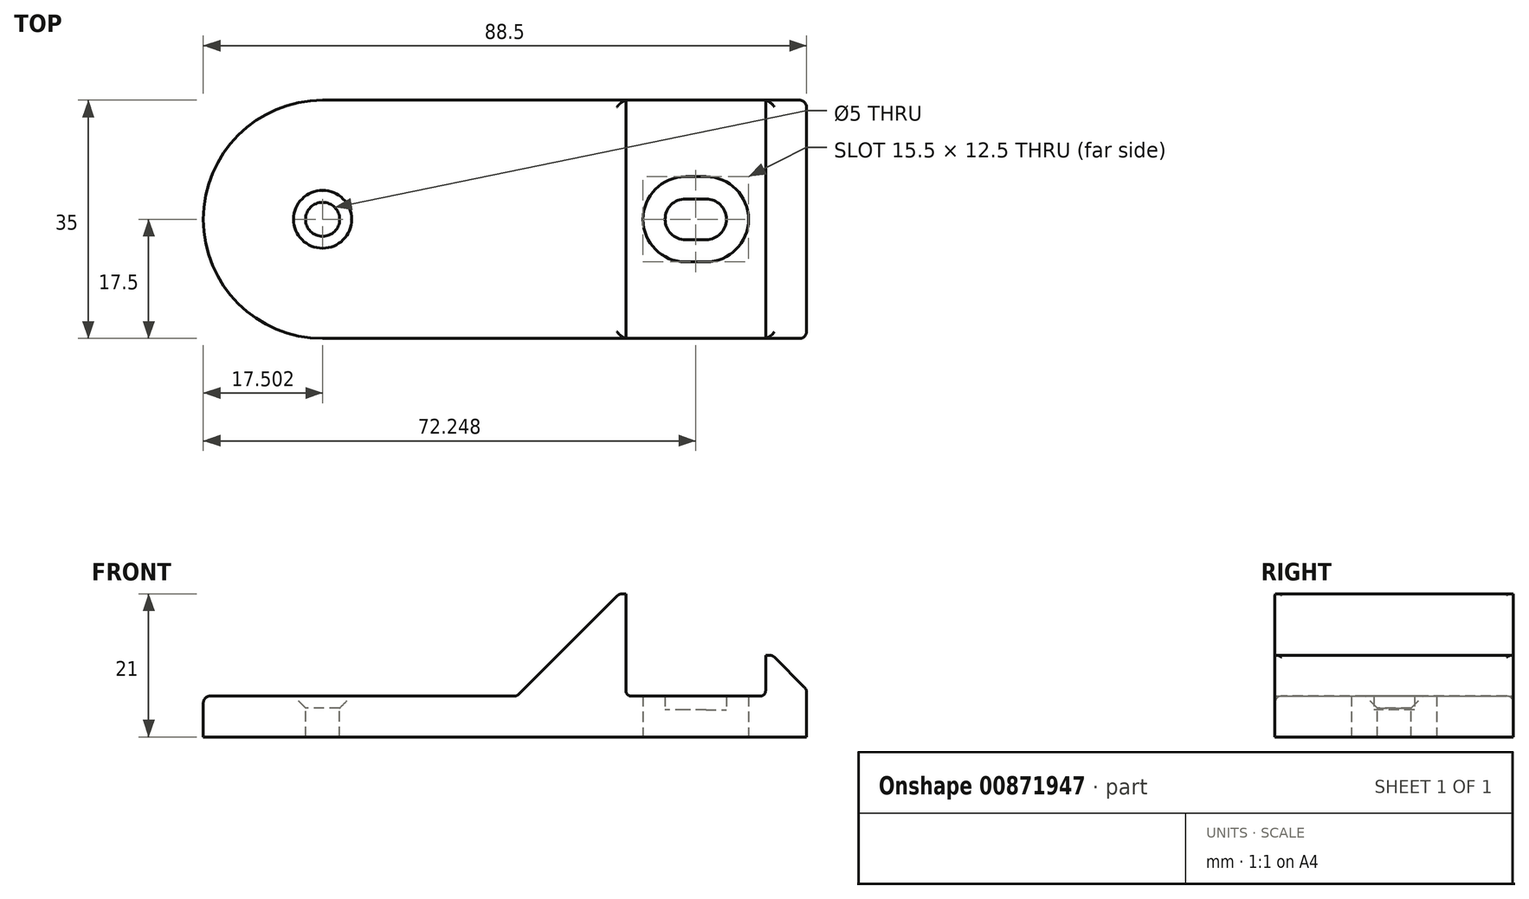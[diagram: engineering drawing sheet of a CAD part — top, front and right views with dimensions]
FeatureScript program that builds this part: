
annotation { "Feature Type Name" : "Feature", "Feature Type Description" : "" }
export const myFeature = defineFeature(function(context is Context, id is Id, definition is map)
    precondition{}
    {
        {
            var Q0;
            Q0=qCreatedBy(makeId("Top.planeOp"),FACE);
            var sketch = newSketch(context, id + "F0", { "sketchPlane" : qUnion([Q0])});
            skLineSegment(sketch, "E0", {"start": v(-55.44, 0) * mm, "end": v(55.68, 0) * mm, "construction": true});
            skLineSegment(sketch, "E1", {"start": v(0, 54) * mm, "end": v(0, -52.34) * mm, "construction": true});
            skLineSegment(sketch, "E2.bottom", {"start": v(-35.65, 17.5) * mm, "end": v(29.35, 17.5) * mm});
            skLineSegment(sketch, "E2.top", {"start": v(-35.65, -17.5) * mm, "end": v(29.35, -17.5) * mm});
            skLineSegment(sketch, "E2.left", {"start": v(-35.65, 17.5) * mm, "end": v(-35.65, -17.5) * mm});
            skLineSegment(sketch, "E2.right", {"start": v(29.35, 17.5) * mm, "end": v(29.35, -17.5) * mm});
            skPoint(sketch, "E3", {"position": v(-35.65, 0) * mm});
            skArc(sketch, "E4", {"start": v(-35.65, -17.5) * mm, "mid": v(-53.15, 0) * mm, "end": v(-35.65, 17.5) * mm});
            skLineSegment(sketch, "E5.bottom", {"start": v(29.35, 17.5) * mm, "end": v(35.35, 17.5) * mm});
            skLineSegment(sketch, "E5.top", {"start": v(29.35, -17.5) * mm, "end": v(35.35, -17.5) * mm});
            skLineSegment(sketch, "E5.right", {"start": v(35.35, 17.5) * mm, "end": v(35.35, -17.5) * mm});
            skLineSegment(sketch, "E6.bottom", {"start": v(8.85, 17.5) * mm, "end": v(2.85, 17.5) * mm});
            skLineSegment(sketch, "E6.top", {"start": v(8.85, -17.5) * mm, "end": v(2.85, -17.5) * mm});
            skLineSegment(sketch, "E6.left", {"start": v(8.85, 17.5) * mm, "end": v(8.85, -17.5) * mm});
            skLineSegment(sketch, "E6.right", {"start": v(2.85, 17.5) * mm, "end": v(2.85, -17.5) * mm});
            skSolve(sketch);
        }
        {
            var Q0;
            {var subQ0=sQuery(id+"F0.wireOp",EDGE,"E6.left");var subQ5=makeQuery(id+"F0.imprint","IMPRINT",EDGE,{"derivedFrom":subQ0});var subQ11=sQuery(id+"F0.wireOp",EDGE,"E2.right");var subQ13=makeQuery(id+"F0.imprint","IMPRINT",EDGE,{"derivedFrom":subQ11});var subQ15=sQuery(id+"F0.wireOp",EDGE,"E2.left");var subQ16=makeQuery(id+"F0.imprint","IMPRINT",EDGE,{"derivedFrom":subQ15});Q0=qUnion([makeQuery(id+"F0.imprint","IMPRINT",FACE,{"disambiguationData":[TD([[subQ16,-1.0]])]}),makeQuery(id+"F0.imprint","IMPRINT",FACE,{"disambiguationData":[TD([[subQ13,1.0]])]}),makeQuery(id+"F0.imprint","IMPRINT",FACE,{"disambiguationData":[TD([[subQ16,1.0]])]}),makeQuery(id+"F0.imprint","IMPRINT",FACE,{"disambiguationData":[TD([[subQ13,-1.0]])]}),makeQuery(id+"F0.imprint","IMPRINT",FACE,{"disambiguationData":[TD([[subQ5,-1.0]])]})]);}
            extrude(context, id + "F1", {"entities" : qUnion([Q0]), "depth" : 6 * mm, "offsetDistance" : 25 * mm});
        }
        {
            var Q0;
            Q0=makeQuery(id+"F0.imprint","IMPRINT",FACE,{"disambiguationData":[TD([[makeQuery(id+"F0.imprint","IMPRINT",EDGE,{"derivedFrom":sQuery(id+"F0.wireOp",EDGE,"E2.right")}),1.0]])]});
            extrude(context, id + "F2", {"entities" : qUnion([Q0]), "operationType" : NewBodyOperationType.ADD, "depth" : 12 * mm, "offsetDistance" : 25 * mm});
        }
        {
            var Q0;
            Q0=makeQuery(id+"F2.opExtrude","CAP_EDGE",EDGE,{"disambiguationData":[OSD([sQuery(id+"F0.wireOp",EDGE,"E5.right")])],"isStart":false});
            chamfer(context, id + "F3", {"entities" : qUnion([Q0]), "width" : 5 * mm, "tangentPropagation" : true});
        }
        {
            var Q0;
            {var subQ0=sQuery(id+"F0.wireOp",EDGE,"E6.left");Q0=makeQuery(id+"F0.imprint","IMPRINT",FACE,{"disambiguationData":[TD([[makeQuery(id+"F0.imprint","IMPRINT",EDGE,{"derivedFrom":subQ0}),-1.0]])]});}
            extrude(context, id + "F4", {"entities" : qUnion([Q0]), "operationType" : NewBodyOperationType.ADD, "depth" : 21 * mm, "offsetDistance" : 25 * mm});
        }
        {
            var Q0;
            Q0=makeQuery(id+"F4.opExtrude","CAP_EDGE",EDGE,{"disambiguationData":[OSD([sQuery(id+"F0.wireOp",EDGE,"E6.right")])],"isStart":false});
            chamfer(context, id + "F5", {"entities" : qUnion([Q0]), "width" : 5 * mm, "tangentPropagation" : true});
        }
        {
            var Q0;
            Q0=makeQuery(id+"F4.opExtrude","SWEPT_FACE",FACE,{"disambiguationData":[OSD([sQuery(id+"F0.wireOp",EDGE,"E6.right")])]});
            extrude(context, id + "F6", {"entities" : qUnion([Q0]), "operationType" : NewBodyOperationType.ADD, "depth" : 12 * mm, "offsetDistance" : 25 * mm});
        }
        {
            var Q0;
            Q0=makeQuery(id+"F6.opExtrude","CAP_EDGE",EDGE,{"disambiguationData":[OSD([sQuery(id+"F0.wireOp",EDGE,"E6.right")])],"isStart":false});
            chamfer(context, id + "F7", {"entities" : qUnion([Q0]), "width" : 12 * mm, "tangentPropagation" : true});
        }
        {
            var Q0;
            {var subQ0=sQuery(id+"F0.wireOp",EDGE,"E5.top");var subQ1=sQuery(id+"F0.wireOp",EDGE,"E2.top");var subQ2=sQuery(id+"F0.wireOp",EDGE,"E4");Q0=makeQuery(id+"F4.boolean.opBoolean","SPLIT",EDGE,{"disambiguationData":[TD([makeQuery(id+"F1.opExtrude","SWEPT_FACE",FACE,{"disambiguationData":[OSD([subQ2])]})])],"derivedFrom":makeQuery(id+"F1.opExtrude","CAP_EDGE",EDGE,{"disambiguationData":[OSD([subQ1,subQ0])],"isStart":false})});}
            var Q1;
            {var subQ0=sQuery(id+"F0.wireOp",EDGE,"E5.right");var subQ1=sQuery(id+"F0.wireOp",EDGE,"E5.top");Q1=makeQuery(id+"F2.boolean.opBoolean","MERGE",EDGE,{"derivedFrom":[makeQuery(id+"F1.opExtrude","SWEPT_EDGE",EDGE,{"disambiguationData":[OSD([subQ1,subQ0])]}),makeQuery(id+"F2.opExtrude","SWEPT_EDGE",EDGE,{"disambiguationData":[OSD([subQ1,subQ0])]})]});}
            var Q2;
            {var subQ0=sQuery(id+"F0.wireOp",EDGE,"E5.top");Q2=makeQuery(id+"F3.opChamfer","BLEND_EDGE",EDGE,{"blendedFrom":[makeQuery(id+"F2.opExtrude","CAP_EDGE",EDGE,{"disambiguationData":[OSD([sQuery(id+"F0.wireOp",EDGE,"E5.right")])],"isStart":false}),makeQuery(id+"F2.boolean.opBoolean","MERGE",FACE,{"derivedFrom":[makeQuery(id+"F1.opExtrude","SWEPT_FACE",FACE,{"disambiguationData":[OSD([sQuery(id+"F0.wireOp",EDGE,"E2.top"),subQ0])]}),makeQuery(id+"F2.opExtrude","SWEPT_FACE",FACE,{"disambiguationData":[OSD([subQ0])]})]})],"blendedInto":[makeQuery(id+"F2.boolean.opBoolean","MERGE",FACE,{"derivedFrom":[makeQuery(id+"F1.opExtrude","SWEPT_FACE",FACE,{"disambiguationData":[OSD([sQuery(id+"F0.wireOp",EDGE,"E2.top"),subQ0])]}),makeQuery(id+"F2.opExtrude","SWEPT_FACE",FACE,{"disambiguationData":[OSD([subQ0])]})]})]});}
            var Q3;
            {var subQ0=sQuery(id+"F0.wireOp",EDGE,"E5.right");Q3=makeQuery(id+"F3.opChamfer","BLEND_EDGE",EDGE,{"blendedFrom":[makeQuery(id+"F2.opExtrude","CAP_EDGE",EDGE,{"disambiguationData":[OSD([subQ0])],"isStart":false}),makeQuery(id+"F2.boolean.opBoolean","MERGE",FACE,{"derivedFrom":[makeQuery(id+"F1.opExtrude","SWEPT_FACE",FACE,{"disambiguationData":[OSD([subQ0])]}),makeQuery(id+"F2.opExtrude","SWEPT_FACE",FACE,{"disambiguationData":[OSD([subQ0])]})]})],"blendedInto":[makeQuery(id+"F2.boolean.opBoolean","MERGE",FACE,{"derivedFrom":[makeQuery(id+"F1.opExtrude","SWEPT_FACE",FACE,{"disambiguationData":[OSD([subQ0])]}),makeQuery(id+"F2.opExtrude","SWEPT_FACE",FACE,{"disambiguationData":[OSD([subQ0])]})]})]});}
            var Q4;
            {var subQ0=sQuery(id+"F0.wireOp",EDGE,"E5.bottom");Q4=makeQuery(id+"F3.opChamfer","BLEND_EDGE",EDGE,{"blendedFrom":[makeQuery(id+"F2.opExtrude","CAP_EDGE",EDGE,{"disambiguationData":[OSD([sQuery(id+"F0.wireOp",EDGE,"E5.right")])],"isStart":false}),makeQuery(id+"F2.boolean.opBoolean","MERGE",FACE,{"derivedFrom":[makeQuery(id+"F1.opExtrude","SWEPT_FACE",FACE,{"disambiguationData":[OSD([sQuery(id+"F0.wireOp",EDGE,"E2.bottom"),subQ0])]}),makeQuery(id+"F2.opExtrude","SWEPT_FACE",FACE,{"disambiguationData":[OSD([subQ0])]})]})],"blendedInto":[makeQuery(id+"F2.boolean.opBoolean","MERGE",FACE,{"derivedFrom":[makeQuery(id+"F1.opExtrude","SWEPT_FACE",FACE,{"disambiguationData":[OSD([sQuery(id+"F0.wireOp",EDGE,"E2.bottom"),subQ0])]}),makeQuery(id+"F2.opExtrude","SWEPT_FACE",FACE,{"disambiguationData":[OSD([subQ0])]})]})]});}
            var Q5;
            {var subQ0=sQuery(id+"F0.wireOp",EDGE,"E5.right");var subQ1=sQuery(id+"F0.wireOp",EDGE,"E5.bottom");Q5=makeQuery(id+"F2.boolean.opBoolean","MERGE",EDGE,{"derivedFrom":[makeQuery(id+"F1.opExtrude","SWEPT_EDGE",EDGE,{"disambiguationData":[OSD([subQ1,subQ0])]}),makeQuery(id+"F2.opExtrude","SWEPT_EDGE",EDGE,{"disambiguationData":[OSD([subQ1,subQ0])]})]});}
            var Q6;
            {var subQ0=sQuery(id+"F0.wireOp",EDGE,"E6.right");var subQ1=sQuery(id+"F0.wireOp",EDGE,"E2.top");var subQ2=sQuery(id+"F0.wireOp",EDGE,"E5.top");Q6=makeQuery(id+"F7.opChamfer","BLEND_EDGE",EDGE,{"blendedFrom":[makeQuery(id+"F6.opExtrude","CAP_EDGE",EDGE,{"disambiguationData":[OSD([subQ0])],"isStart":false}),makeQuery(id+"F6.boolean.opBoolean","MERGE",FACE,{"derivedFrom":[makeQuery(id+"F4.boolean.opBoolean","MERGE",FACE,{"derivedFrom":[makeQuery(id+"F2.boolean.opBoolean","MERGE",FACE,{"derivedFrom":[makeQuery(id+"F1.opExtrude","SWEPT_FACE",FACE,{"disambiguationData":[OSD([subQ1,subQ2])]}),makeQuery(id+"F2.opExtrude","SWEPT_FACE",FACE,{"disambiguationData":[OSD([subQ2])]})]}),makeQuery(id+"F4.opExtrude","SWEPT_FACE",FACE,{"disambiguationData":[OSD([subQ1])]})]}),makeQuery(id+"F6.opExtrude","SWEPT_FACE",FACE,{"disambiguationData":[OSD([subQ1,subQ0])]})]})],"blendedInto":[makeQuery(id+"F6.boolean.opBoolean","MERGE",FACE,{"derivedFrom":[makeQuery(id+"F4.boolean.opBoolean","MERGE",FACE,{"derivedFrom":[makeQuery(id+"F2.boolean.opBoolean","MERGE",FACE,{"derivedFrom":[makeQuery(id+"F1.opExtrude","SWEPT_FACE",FACE,{"disambiguationData":[OSD([subQ1,subQ2])]}),makeQuery(id+"F2.opExtrude","SWEPT_FACE",FACE,{"disambiguationData":[OSD([subQ2])]})]}),makeQuery(id+"F4.opExtrude","SWEPT_FACE",FACE,{"disambiguationData":[OSD([subQ1])]})]}),makeQuery(id+"F6.opExtrude","SWEPT_FACE",FACE,{"disambiguationData":[OSD([subQ1,subQ0])]})]})]});}
            var Q7;
            {var subQ0=sQuery(id+"F0.wireOp",EDGE,"E6.right");var subQ1=sQuery(id+"F0.wireOp",EDGE,"E2.bottom");var subQ2=sQuery(id+"F0.wireOp",EDGE,"E5.bottom");Q7=makeQuery(id+"F7.opChamfer","BLEND_EDGE",EDGE,{"blendedFrom":[makeQuery(id+"F6.opExtrude","CAP_EDGE",EDGE,{"disambiguationData":[OSD([subQ0])],"isStart":false}),makeQuery(id+"F6.boolean.opBoolean","MERGE",FACE,{"derivedFrom":[makeQuery(id+"F4.boolean.opBoolean","MERGE",FACE,{"derivedFrom":[makeQuery(id+"F2.boolean.opBoolean","MERGE",FACE,{"derivedFrom":[makeQuery(id+"F1.opExtrude","SWEPT_FACE",FACE,{"disambiguationData":[OSD([subQ1,subQ2])]}),makeQuery(id+"F2.opExtrude","SWEPT_FACE",FACE,{"disambiguationData":[OSD([subQ2])]})]}),makeQuery(id+"F4.opExtrude","SWEPT_FACE",FACE,{"disambiguationData":[OSD([subQ1])]})]}),makeQuery(id+"F6.opExtrude","SWEPT_FACE",FACE,{"disambiguationData":[OSD([subQ1,subQ0])]})]})],"blendedInto":[makeQuery(id+"F6.boolean.opBoolean","MERGE",FACE,{"derivedFrom":[makeQuery(id+"F4.boolean.opBoolean","MERGE",FACE,{"derivedFrom":[makeQuery(id+"F2.boolean.opBoolean","MERGE",FACE,{"derivedFrom":[makeQuery(id+"F1.opExtrude","SWEPT_FACE",FACE,{"disambiguationData":[OSD([subQ1,subQ2])]}),makeQuery(id+"F2.opExtrude","SWEPT_FACE",FACE,{"disambiguationData":[OSD([subQ2])]})]}),makeQuery(id+"F4.opExtrude","SWEPT_FACE",FACE,{"disambiguationData":[OSD([subQ1])]})]}),makeQuery(id+"F6.opExtrude","SWEPT_FACE",FACE,{"disambiguationData":[OSD([subQ1,subQ0])]})]})]});}
            var Q8;
            {var subQ0=sQuery(id+"F0.wireOp",EDGE,"E2.bottom");var subQ1=sQuery(id+"F0.wireOp",EDGE,"E5.bottom");Q8=makeQuery(id+"F5.opChamfer","BLEND_EDGE",EDGE,{"blendedFrom":[makeQuery(id+"F4.opExtrude","CAP_EDGE",EDGE,{"disambiguationData":[OSD([sQuery(id+"F0.wireOp",EDGE,"E6.right")])],"isStart":false}),makeQuery(id+"F4.boolean.opBoolean","MERGE",FACE,{"derivedFrom":[makeQuery(id+"F2.boolean.opBoolean","MERGE",FACE,{"derivedFrom":[makeQuery(id+"F1.opExtrude","SWEPT_FACE",FACE,{"disambiguationData":[OSD([subQ0,subQ1])]}),makeQuery(id+"F2.opExtrude","SWEPT_FACE",FACE,{"disambiguationData":[OSD([subQ1])]})]}),makeQuery(id+"F4.opExtrude","SWEPT_FACE",FACE,{"disambiguationData":[OSD([subQ0])]})]})],"blendedInto":[makeQuery(id+"F4.boolean.opBoolean","MERGE",FACE,{"derivedFrom":[makeQuery(id+"F2.boolean.opBoolean","MERGE",FACE,{"derivedFrom":[makeQuery(id+"F1.opExtrude","SWEPT_FACE",FACE,{"disambiguationData":[OSD([subQ0,subQ1])]}),makeQuery(id+"F2.opExtrude","SWEPT_FACE",FACE,{"disambiguationData":[OSD([subQ1])]})]}),makeQuery(id+"F4.opExtrude","SWEPT_FACE",FACE,{"disambiguationData":[OSD([subQ0])]})]})]});}
            var Q9;
            {var subQ0=sQuery(id+"F0.wireOp",EDGE,"E5.right");Q9=makeQuery(id+"F3.opChamfer","BLEND_EDGE",EDGE,{"blendedFrom":[makeQuery(id+"F2.opExtrude","CAP_EDGE",EDGE,{"disambiguationData":[OSD([subQ0])],"isStart":false}),makeQuery(id+"F2.opExtrude","CAP_FACE",FACE,{"disambiguationData":[OSD([sQuery(id+"F0.wireOp",EDGE,"E2.right"),sQuery(id+"F0.wireOp",EDGE,"E5.bottom"),sQuery(id+"F0.wireOp",EDGE,"E5.top"),subQ0])],"isStart":false})],"blendedInto":[makeQuery(id+"F2.opExtrude","CAP_FACE",FACE,{"disambiguationData":[OSD([sQuery(id+"F0.wireOp",EDGE,"E2.right"),sQuery(id+"F0.wireOp",EDGE,"E5.bottom"),sQuery(id+"F0.wireOp",EDGE,"E5.top"),subQ0])],"isStart":false})]});}
            var Q10;
            {var subQ0=sQuery(id+"F0.wireOp",EDGE,"E6.right");Q10=makeQuery(id+"F5.opChamfer","BLEND_EDGE",EDGE,{"blendedFrom":[makeQuery(id+"F4.opExtrude","CAP_EDGE",EDGE,{"disambiguationData":[OSD([subQ0])],"isStart":false}),makeQuery(id+"F4.opExtrude","CAP_FACE",FACE,{"disambiguationData":[OSD([sQuery(id+"F0.wireOp",EDGE,"E2.bottom"),sQuery(id+"F0.wireOp",EDGE,"E2.top"),sQuery(id+"F0.wireOp",EDGE,"E6.left"),subQ0])],"isStart":false})],"blendedInto":[makeQuery(id+"F4.opExtrude","CAP_FACE",FACE,{"disambiguationData":[OSD([sQuery(id+"F0.wireOp",EDGE,"E2.bottom"),sQuery(id+"F0.wireOp",EDGE,"E2.top"),sQuery(id+"F0.wireOp",EDGE,"E6.left"),subQ0])],"isStart":false})]});}
            var Q11;
            {var subQ0=sQuery(id+"F0.wireOp",EDGE,"E5.bottom");var subQ1=sQuery(id+"F0.wireOp",EDGE,"E4");var subQ2=sQuery(id+"F0.wireOp",EDGE,"E5.top");var subQ3=sQuery(id+"F0.wireOp",EDGE,"E2.top");var subQ4=sQuery(id+"F0.wireOp",EDGE,"E2.bottom");var subQ5=sQuery(id+"F0.wireOp",EDGE,"E6.right");Q11=makeQuery(id+"F7.opChamfer","BLEND_EDGE",EDGE,{"blendedFrom":[makeQuery(id+"F6.opExtrude","CAP_EDGE",EDGE,{"disambiguationData":[OSD([subQ5])],"isStart":false}),makeQuery(id+"F4.boolean.opBoolean","SPLIT",FACE,{"disambiguationData":[TD([makeQuery(id+"F1.opExtrude","SWEPT_FACE",FACE,{"disambiguationData":[OSD([subQ1])]})])],"derivedFrom":makeQuery(id+"F1.opExtrude","CAP_FACE",FACE,{"disambiguationData":[OSD([subQ4,subQ3,subQ1,subQ0,subQ2,sQuery(id+"F0.wireOp",EDGE,"E5.right")])],"isStart":false})})],"blendedInto":[makeQuery(id+"F4.boolean.opBoolean","SPLIT",FACE,{"disambiguationData":[TD([makeQuery(id+"F1.opExtrude","SWEPT_FACE",FACE,{"disambiguationData":[OSD([subQ1])]})])],"derivedFrom":makeQuery(id+"F1.opExtrude","CAP_FACE",FACE,{"disambiguationData":[OSD([subQ4,subQ3,subQ1,subQ0,subQ2,sQuery(id+"F0.wireOp",EDGE,"E5.right")])],"isStart":false})})]});}
            fillet(context, id + "F8", {"entities" : qUnion([Q0, Q1, Q2, Q3, Q4, Q5, Q6, Q7, Q8, Q9, Q10, Q11]), "radius" : 1 * mm, "tangentPropagation" : true, "allowEdgeOverflow" : false});
        }
        {
            var Q0;
            Q0=makeQuery(id+"F4.boolean.opBoolean","INTERSECT",EDGE,{"derivedFrom":[makeQuery(id+"F1.opExtrude","CAP_FACE",FACE,{"disambiguationData":[OSD([sQuery(id+"F0.wireOp",EDGE,"E2.bottom"),sQuery(id+"F0.wireOp",EDGE,"E2.top"),sQuery(id+"F0.wireOp",EDGE,"E4"),sQuery(id+"F0.wireOp",EDGE,"E5.bottom"),sQuery(id+"F0.wireOp",EDGE,"E5.top"),sQuery(id+"F0.wireOp",EDGE,"E5.right")])],"isStart":false}),makeQuery(id+"F4.opExtrude","SWEPT_FACE",FACE,{"disambiguationData":[OSD([sQuery(id+"F0.wireOp",EDGE,"E6.left")])]})]});
            var Q1;
            Q1=makeQuery(id+"F2.boolean.opBoolean","INTERSECT",EDGE,{"derivedFrom":[makeQuery(id+"F1.opExtrude","CAP_FACE",FACE,{"disambiguationData":[OSD([sQuery(id+"F0.wireOp",EDGE,"E2.bottom"),sQuery(id+"F0.wireOp",EDGE,"E2.top"),sQuery(id+"F0.wireOp",EDGE,"E4"),sQuery(id+"F0.wireOp",EDGE,"E5.bottom"),sQuery(id+"F0.wireOp",EDGE,"E5.top"),sQuery(id+"F0.wireOp",EDGE,"E5.right")])],"isStart":false}),makeQuery(id+"F2.opExtrude","SWEPT_FACE",FACE,{"disambiguationData":[OSD([sQuery(id+"F0.wireOp",EDGE,"E2.right")])]})]});
            fillet(context, id + "F9", {"entities" : qUnion([Q0, Q1]), "radius" : 0.8 * mm, "allowEdgeOverflow" : false});
        }
        {
            var Q0;
            {var subQ0=sQuery(id+"F0.wireOp",EDGE,"E5.bottom");var subQ1=sQuery(id+"F0.wireOp",EDGE,"E4");var subQ2=sQuery(id+"F0.wireOp",EDGE,"E5.top");var subQ3=sQuery(id+"F0.wireOp",EDGE,"E2.top");var subQ4=sQuery(id+"F0.wireOp",EDGE,"E2.bottom");Q0=makeQuery(id+"F4.boolean.opBoolean","SPLIT",FACE,{"disambiguationData":[TD([makeQuery(id+"F1.opExtrude","SWEPT_FACE",FACE,{"disambiguationData":[OSD([subQ1])]})])],"derivedFrom":makeQuery(id+"F1.opExtrude","CAP_FACE",FACE,{"disambiguationData":[OSD([subQ4,subQ3,subQ1,subQ0,subQ2,sQuery(id+"F0.wireOp",EDGE,"E5.right")])],"isStart":false})});}
            var sketch = newSketch(context, id + "F10", { "sketchPlane" : qUnion([Q0])});
            skPoint(sketch, "E7", {"position": v(-35.65, 0) * mm});
            skSolve(sketch);
        }
        {
            assignVariable(context, id + "F11", {"name" : "screw_wood_diameter", "anyValue" : 4});
        }
        {
            var Q0;
            Q0=sQuery(id+"F10.wireOp",VERTEX,"E7");
            var Q1;
            Q1=makeQuery(id+"F1.opExtrude","SWEPT_BODY",BODY,{"disambiguationData":[OSD([sQuery(id+"F0.wireOp",EDGE,"E2.bottom"),sQuery(id+"F0.wireOp",EDGE,"E2.top"),sQuery(id+"F0.wireOp",EDGE,"E4"),sQuery(id+"F0.wireOp",EDGE,"E5.bottom"),sQuery(id+"F0.wireOp",EDGE,"E5.top"),sQuery(id+"F0.wireOp",EDGE,"E5.right")])]});
            hole(context, id + "F12", {"style" : HoleStyle.C_SINK, "endStyle" : HoleEndStyle.THROUGH, "holeDiameter" : (getVariable(context, 'screw_wood_diameter') + 1) * mm, "cSinkDiameter" : (getVariable(context, 'screw_wood_diameter') * 2 + 0.5) * mm, "cSinkAngle" : 90 * degree, "majorDiameter" : 5 * mm, "isTappedThrough" : true, "tappedDepth" : 12 * mm, "tapClearance" : 3, "locations" : qUnion([Q0]), "scope" : qUnion([Q1])});
        }
        {
            var Q0;
            {var subQ2=sQuery(id+"F0.wireOp",EDGE,"E2.right");Q0=makeQuery(id+"F0.imprint","IMPRINT",FACE,{"disambiguationData":[TD([[makeQuery(id+"F0.imprint","IMPRINT",EDGE,{"derivedFrom":subQ2}),-1.0]])]});}
            var sketch = newSketch(context, id + "F13", { "sketchPlane" : qUnion([Q0])});
            skPoint(sketch, "E8", {"position": v(19.1, 0) * mm});
            skPoint(sketch, "E8.positionSnap0", {"position": v(19.1, 17.5) * mm});
            skLineSegment(sketch, "E9", {"start": v(20.6, 0) * mm, "end": v(17.6, 0) * mm, "construction": true});
            skArc(sketch, "E10.0.startCap", {"start": v(20.6, 3) * mm, "mid": v(23.6, 0) * mm, "end": v(20.6, -3) * mm});
            skArc(sketch, "E10.0.endCap", {"start": v(17.6, -3) * mm, "mid": v(14.6, 0) * mm, "end": v(17.6, 3) * mm});
            skLineSegment(sketch, "E10.0.left", {"start": v(20.6, -3) * mm, "end": v(17.6, -3) * mm});
            skLineSegment(sketch, "E10.0.right", {"start": v(20.6, 3) * mm, "end": v(17.6, 3) * mm});
            skArc(sketch, "E11.0.startCap", {"start": v(20.6, 6.25) * mm, "mid": v(26.85, 0) * mm, "end": v(20.6, -6.25) * mm});
            skArc(sketch, "E11.0.endCap", {"start": v(17.6, -6.25) * mm, "mid": v(11.35, 0) * mm, "end": v(17.6, 6.25) * mm});
            skLineSegment(sketch, "E11.0.left", {"start": v(20.6, -6.25) * mm, "end": v(17.6, -6.25) * mm});
            skLineSegment(sketch, "E11.0.right", {"start": v(20.6, 6.25) * mm, "end": v(17.6, 6.25) * mm});
            skSolve(sketch);
        }
        {
            var Q0;
            Q0=makeQuery(id+"F13.imprint","IMPRINT",FACE,{"disambiguationData":[TD([[makeQuery(id+"F13.imprint","IMPRINT",EDGE,{"derivedFrom":sQuery(id+"F13.wireOp",EDGE,"E10.0.startCap")}),-1.0]])]});
            extrude(context, id + "F14", {"entities" : qUnion([Q0]), "operationType" : NewBodyOperationType.REMOVE, "endBound" : BoundingType.UP_TO_NEXT, "depth" : 25 * mm, "offsetDistance" : 25 * mm});
        }
        {
            var Q0;
            Q0=makeQuery(id+"F13.imprint","IMPRINT",FACE,{"disambiguationData":[TD([[makeQuery(id+"F13.imprint","IMPRINT",EDGE,{"derivedFrom":sQuery(id+"F13.wireOp",EDGE,"E10.0.startCap")}),1.0]])]});
            extrude(context, id + "F15", {"entities" : qUnion([Q0]), "operationType" : NewBodyOperationType.REMOVE, "depth" : 4 * mm, "offsetDistance" : 25 * mm});
        }
    });
